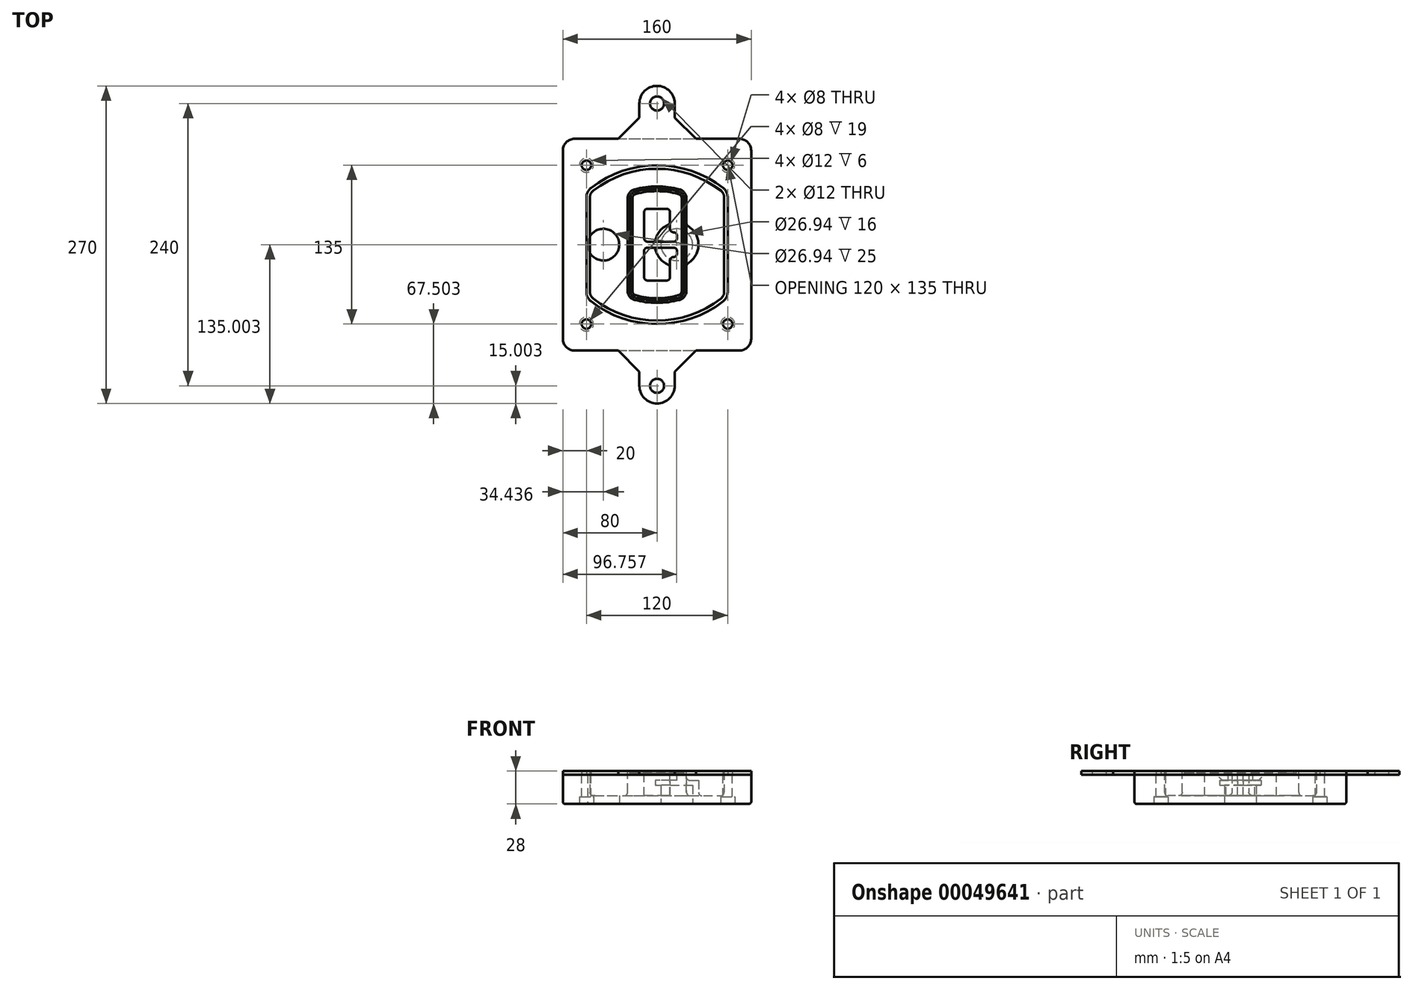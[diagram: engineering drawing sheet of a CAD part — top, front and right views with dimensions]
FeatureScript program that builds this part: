
annotation { "Feature Type Name" : "Feature", "Feature Type Description" : "" }
export const myFeature = defineFeature(function(context is Context, id is Id, definition is map)
    precondition{}
    {
        {
            var Q0;
            Q0=qCreatedBy(makeId("Top.planeOp"),FACE);
            var sketch = newSketch(context, id + "F0", { "sketchPlane" : qUnion([Q0])});
            skPoint(sketch, "E0.rect.middle", {"position": v(0, 0) * mm});
            skLineSegment(sketch, "E1.bottom", {"start": v(24.05, 28.38) * mm, "end": v(164.05, 28.38) * mm});
            skLineSegment(sketch, "E1.top", {"start": v(24.05, 208.38) * mm, "end": v(164.05, 208.38) * mm});
            skLineSegment(sketch, "E1.left", {"start": v(14.05, 38.38) * mm, "end": v(14.05, 198.38) * mm});
            skLineSegment(sketch, "E1.right", {"start": v(174.05, 38.38) * mm, "end": v(174.05, 198.38) * mm});
            skLineSegment(sketch, "E2", {"start": v(14.05, 208.38) * mm, "end": v(174.05, 28.38) * mm, "construction": true});
            skLineSegment(sketch, "E3", {"start": v(174.05, 208.38) * mm, "end": v(14.05, 28.38) * mm, "construction": true});
            skCircle(sketch, "E4", {"center": v(34.05, 185.88) * mm, "radius": 4 * mm});
            skCircle(sketch, "E5", {"center": v(154.05, 185.88) * mm, "radius": 4 * mm});
            skCircle(sketch, "E6", {"center": v(154.05, 50.88) * mm, "radius": 4 * mm});
            skCircle(sketch, "E7", {"center": v(34.05, 50.88) * mm, "radius": 4 * mm});
            skLineSegment(sketch, "E8", {"start": v(34.05, 185.88) * mm, "end": v(154.05, 185.88) * mm, "construction": true});
            skLineSegment(sketch, "E9", {"start": v(154.05, 185.88) * mm, "end": v(154.05, 50.88) * mm, "construction": true});
            skLineSegment(sketch, "E10", {"start": v(154.05, 50.88) * mm, "end": v(34.05, 50.88) * mm, "construction": true});
            skLineSegment(sketch, "E11", {"start": v(34.05, 50.88) * mm, "end": v(34.05, 185.88) * mm, "construction": true});
            skLineSegment(sketch, "E12", {"start": v(34.05, 158.68) * mm, "end": v(34.05, 78.09) * mm});
            skLineSegment(sketch, "E13", {"start": v(154.05, 158.68) * mm, "end": v(154.05, 78.09) * mm});
            skArc(sketch, "E14", {"start": v(150.2, 166.56) * mm, "mid": v(94.05, 185.88) * mm, "end": v(37.9, 166.56) * mm});
            skArc(sketch, "E15", {"start": v(37.9, 70.2) * mm, "mid": v(94.05, 50.88) * mm, "end": v(150.2, 70.2) * mm});
            skLineSegment(sketch, "E16", {"start": v(34.05, 118.38) * mm, "end": v(154.05, 118.38) * mm, "construction": true});
            skPoint(sketch, "E17.visualSharp", {"position": v(34.05, 73.38) * mm});
            skArc(sketch, "E17.filletArc", {"start": v(34.05, 78.09) * mm, "mid": v(35.06, 73.7) * mm, "end": v(37.9, 70.2) * mm});
            skPoint(sketch, "E18.visualSharp", {"position": v(34.05, 163.38) * mm});
            skArc(sketch, "E18.filletArc", {"start": v(37.9, 166.56) * mm, "mid": v(35.06, 163.06) * mm, "end": v(34.05, 158.68) * mm});
            skPoint(sketch, "E19.visualSharp", {"position": v(154.05, 163.38) * mm});
            skArc(sketch, "E19.filletArc", {"start": v(154.05, 158.68) * mm, "mid": v(153.04, 163.06) * mm, "end": v(150.2, 166.56) * mm});
            skPoint(sketch, "E20.visualSharp", {"position": v(154.05, 73.38) * mm});
            skArc(sketch, "E20.filletArc", {"start": v(150.2, 70.2) * mm, "mid": v(153.04, 73.7) * mm, "end": v(154.05, 78.09) * mm});
            skPoint(sketch, "E21.visualSharp", {"position": v(14.05, 208.38) * mm});
            skArc(sketch, "E21.filletArc", {"start": v(24.05, 208.38) * mm, "mid": v(16.98, 205.45) * mm, "end": v(14.05, 198.38) * mm});
            skPoint(sketch, "E22.visualSharp", {"position": v(174.05, 208.38) * mm});
            skArc(sketch, "E22.filletArc", {"start": v(174.05, 198.38) * mm, "mid": v(171.12, 205.45) * mm, "end": v(164.05, 208.38) * mm});
            skPoint(sketch, "E23.visualSharp", {"position": v(174.05, 28.38) * mm});
            skArc(sketch, "E23.filletArc", {"start": v(164.05, 28.38) * mm, "mid": v(171.12, 31.31) * mm, "end": v(174.05, 38.38) * mm});
            skPoint(sketch, "E24.visualSharp", {"position": v(14.05, 28.38) * mm});
            skArc(sketch, "E24.filletArc", {"start": v(14.05, 38.38) * mm, "mid": v(16.98, 31.31) * mm, "end": v(24.05, 28.38) * mm});
            skArc(sketch, "E25.0", {"start": v(151.05, 158.68) * mm, "mid": v(150.34, 161.75) * mm, "end": v(148.36, 164.2) * mm});
            skLineSegment(sketch, "E25.1", {"start": v(151.05, 158.68) * mm, "end": v(151.05, 78.09) * mm});
            skArc(sketch, "E25.2", {"start": v(148.36, 72.57) * mm, "mid": v(150.34, 75.02) * mm, "end": v(151.05, 78.09) * mm});
            skArc(sketch, "E25.3", {"start": v(39.74, 72.57) * mm, "mid": v(94.05, 53.88) * mm, "end": v(148.36, 72.57) * mm});
            skArc(sketch, "E25.4", {"start": v(37.05, 78.09) * mm, "mid": v(37.76, 75.02) * mm, "end": v(39.74, 72.57) * mm});
            skArc(sketch, "E25.5", {"start": v(148.36, 164.2) * mm, "mid": v(94.05, 182.88) * mm, "end": v(39.74, 164.2) * mm});
            skLineSegment(sketch, "E25.6", {"start": v(37.05, 158.68) * mm, "end": v(37.05, 78.09) * mm});
            skArc(sketch, "E25.7", {"start": v(39.74, 164.2) * mm, "mid": v(37.76, 161.75) * mm, "end": v(37.05, 158.68) * mm});
            skArc(sketch, "E26.0", {"start": v(35.43, 169.71) * mm, "mid": v(31.47, 164.82) * mm, "end": v(30.05, 158.68) * mm});
            skArc(sketch, "E26.1", {"start": v(152.67, 169.71) * mm, "mid": v(94.05, 189.88) * mm, "end": v(35.43, 169.71) * mm});
            skArc(sketch, "E26.2", {"start": v(158.05, 158.68) * mm, "mid": v(156.63, 164.82) * mm, "end": v(152.67, 169.71) * mm});
            skLineSegment(sketch, "E26.3", {"start": v(158.05, 158.68) * mm, "end": v(158.05, 78.09) * mm});
            skArc(sketch, "E26.4", {"start": v(152.67, 67.05) * mm, "mid": v(156.63, 71.95) * mm, "end": v(158.05, 78.09) * mm});
            skLineSegment(sketch, "E26.5", {"start": v(30.05, 158.68) * mm, "end": v(30.05, 78.09) * mm});
            skArc(sketch, "E26.6", {"start": v(35.43, 67.05) * mm, "mid": v(94.05, 46.88) * mm, "end": v(152.67, 67.05) * mm});
            skArc(sketch, "E26.7", {"start": v(30.05, 78.09) * mm, "mid": v(31.47, 71.95) * mm, "end": v(35.43, 67.05) * mm});
            skSolve(sketch);
        }
        {
            var Q0;
            Q0=makeQuery(id+"F0.imprint","IMPRINT",FACE,{"disambiguationData":[TD([[makeQuery(id+"F0.imprint","IMPRINT",EDGE,{"derivedFrom":sQuery(id+"F0.wireOp",EDGE,"E1.bottom")}),1.0]])]});
            var Q1;
            Q1=makeQuery(id+"F0.imprint","IMPRINT",FACE,{"disambiguationData":[TD([[makeQuery(id+"F0.imprint","IMPRINT",EDGE,{"derivedFrom":sQuery(id+"F0.wireOp",EDGE,"E12")}),1.0]])]});
            var Q2;
            Q2=makeQuery(id+"F0.imprint","IMPRINT",FACE,{"disambiguationData":[TD([[makeQuery(id+"F0.imprint","IMPRINT",EDGE,{"derivedFrom":sQuery(id+"F0.wireOp",EDGE,"E25.0")}),1.0]])]});
            var Q3;
            Q3=makeQuery(id+"F0.imprint","IMPRINT",FACE,{"disambiguationData":[TD([[makeQuery(id+"F0.imprint","IMPRINT",EDGE,{"derivedFrom":sQuery(id+"F0.wireOp",EDGE,"E12")}),-1.0]])]});
            extrude(context, id + "F1", {"entities" : qUnion([Q0, Q1, Q2, Q3]), "oppositeDirection" : true, "depth" : 25 * mm});
        }
        {
            var Q0;
            Q0=makeQuery(id+"F0.imprint","IMPRINT",FACE,{"disambiguationData":[TD([[makeQuery(id+"F0.imprint","IMPRINT",EDGE,{"derivedFrom":sQuery(id+"F0.wireOp",EDGE,"E12")}),1.0]])]});
            extrude(context, id + "F2", {"entities" : qUnion([Q0]), "operationType" : NewBodyOperationType.ADD, "depth" : 3 * mm});
        }
        {
            var Q0;
            Q0=makeQuery(id+"F0.imprint","IMPRINT",FACE,{"disambiguationData":[TD([[makeQuery(id+"F0.imprint","IMPRINT",EDGE,{"derivedFrom":sQuery(id+"F0.wireOp",EDGE,"E25.0")}),1.0]])]});
            extrude(context, id + "F3", {"entities" : qUnion([Q0]), "operationType" : NewBodyOperationType.REMOVE, "oppositeDirection" : true, "depth" : 18 * mm});
        }
        {
            var Q0;
            Q0=makeQuery(id+"F2.opExtrude","CAP_FACE",FACE,{"disambiguationData":[OSD([sQuery(id+"F0.wireOp",EDGE,"E12"),sQuery(id+"F0.wireOp",EDGE,"E13"),sQuery(id+"F0.wireOp",EDGE,"E14"),sQuery(id+"F0.wireOp",EDGE,"E15"),sQuery(id+"F0.wireOp",EDGE,"E17.filletArc"),sQuery(id+"F0.wireOp",EDGE,"E18.filletArc"),sQuery(id+"F0.wireOp",EDGE,"E19.filletArc"),sQuery(id+"F0.wireOp",EDGE,"E20.filletArc"),sQuery(id+"F0.wireOp",EDGE,"E25.0"),sQuery(id+"F0.wireOp",EDGE,"E25.1"),sQuery(id+"F0.wireOp",EDGE,"E25.2"),sQuery(id+"F0.wireOp",EDGE,"E25.3"),sQuery(id+"F0.wireOp",EDGE,"E25.4"),sQuery(id+"F0.wireOp",EDGE,"E25.5"),sQuery(id+"F0.wireOp",EDGE,"E25.6"),sQuery(id+"F0.wireOp",EDGE,"E25.7")])],"isStart":false});
            var sketch = newSketch(context, id + "F4", { "sketchPlane" : qUnion([Q0])});
            skArc(sketch, "E27.0", {"start": v(74.97, 71.41) * mm, "mid": v(94.05, 68.88) * mm, "end": v(113.13, 71.41) * mm});
            skArc(sketch, "E28.0", {"start": v(113.13, 165.35) * mm, "mid": v(94.05, 167.88) * mm, "end": v(74.97, 165.35) * mm});
            skLineSegment(sketch, "E29", {"start": v(69.05, 157.63) * mm, "end": v(69.05, 79.14) * mm});
            skLineSegment(sketch, "E30", {"start": v(119.05, 157.63) * mm, "end": v(119.05, 79.14) * mm});
            skLineSegment(sketch, "E31", {"start": v(69.05, 163.48) * mm, "end": v(119.05, 163.48) * mm, "construction": true});
            skLineSegment(sketch, "E32", {"start": v(69.05, 73.28) * mm, "end": v(119.05, 73.28) * mm, "construction": true});
            skPoint(sketch, "E33.visualSharp", {"position": v(69.05, 163.48) * mm});
            skArc(sketch, "E33.filletArc", {"start": v(74.97, 165.35) * mm, "mid": v(70.7, 162.5) * mm, "end": v(69.05, 157.63) * mm});
            skPoint(sketch, "E34.visualSharp", {"position": v(119.05, 163.48) * mm});
            skArc(sketch, "E34.filletArc", {"start": v(119.05, 157.63) * mm, "mid": v(117.4, 162.5) * mm, "end": v(113.13, 165.35) * mm});
            skPoint(sketch, "E35.visualSharp", {"position": v(119.05, 73.28) * mm});
            skArc(sketch, "E35.filletArc", {"start": v(113.13, 71.41) * mm, "mid": v(117.4, 74.27) * mm, "end": v(119.05, 79.14) * mm});
            skPoint(sketch, "E36.visualSharp", {"position": v(69.05, 73.28) * mm});
            skArc(sketch, "E36.filletArc", {"start": v(69.05, 79.14) * mm, "mid": v(70.7, 74.27) * mm, "end": v(74.97, 71.41) * mm});
            skArc(sketch, "E37.0", {"start": v(148.36, 164.2) * mm, "mid": v(94.05, 182.88) * mm, "end": v(39.74, 164.2) * mm});
            skArc(sketch, "E37.1", {"start": v(39.74, 164.2) * mm, "mid": v(37.76, 161.75) * mm, "end": v(37.05, 158.68) * mm});
            skLineSegment(sketch, "E37.2", {"start": v(37.05, 158.68) * mm, "end": v(37.05, 78.09) * mm});
            skArc(sketch, "E37.3", {"start": v(37.05, 78.09) * mm, "mid": v(37.76, 75.02) * mm, "end": v(39.74, 72.57) * mm});
            skArc(sketch, "E37.4", {"start": v(39.74, 72.57) * mm, "mid": v(94.05, 53.88) * mm, "end": v(148.36, 72.57) * mm});
            skArc(sketch, "E37.5", {"start": v(148.36, 72.57) * mm, "mid": v(150.34, 75.02) * mm, "end": v(151.05, 78.09) * mm});
            skLineSegment(sketch, "E37.6", {"start": v(151.05, 158.68) * mm, "end": v(151.05, 78.09) * mm});
            skArc(sketch, "E37.7", {"start": v(151.05, 158.68) * mm, "mid": v(150.34, 161.75) * mm, "end": v(148.36, 164.2) * mm});
            skLineSegment(sketch, "E38.0", {"start": v(117.05, 157.63) * mm, "end": v(117.05, 79.14) * mm});
            skArc(sketch, "E38.1", {"start": v(112.61, 73.34) * mm, "mid": v(115.81, 75.49) * mm, "end": v(117.05, 79.14) * mm});
            skArc(sketch, "E38.2", {"start": v(75.49, 73.34) * mm, "mid": v(94.05, 70.88) * mm, "end": v(112.61, 73.34) * mm});
            skArc(sketch, "E38.3", {"start": v(71.05, 79.14) * mm, "mid": v(72.29, 75.49) * mm, "end": v(75.49, 73.34) * mm});
            skLineSegment(sketch, "E38.4", {"start": v(71.05, 157.63) * mm, "end": v(71.05, 79.14) * mm});
            skArc(sketch, "E38.5", {"start": v(117.05, 157.63) * mm, "mid": v(115.81, 161.28) * mm, "end": v(112.61, 163.42) * mm});
            skArc(sketch, "E38.6", {"start": v(75.49, 163.42) * mm, "mid": v(72.29, 161.28) * mm, "end": v(71.05, 157.63) * mm});
            skArc(sketch, "E38.7", {"start": v(112.61, 163.42) * mm, "mid": v(94.05, 165.88) * mm, "end": v(75.49, 163.42) * mm});
            skArc(sketch, "E39.0", {"start": v(115.05, 157.63) * mm, "mid": v(114.23, 160.06) * mm, "end": v(112.1, 161.5) * mm});
            skLineSegment(sketch, "E39.1", {"start": v(115.05, 157.63) * mm, "end": v(115.05, 79.14) * mm});
            skArc(sketch, "E39.2", {"start": v(112.1, 75.27) * mm, "mid": v(114.23, 76.7) * mm, "end": v(115.05, 79.14) * mm});
            skArc(sketch, "E39.3", {"start": v(76, 75.27) * mm, "mid": v(94.05, 72.88) * mm, "end": v(112.1, 75.27) * mm});
            skArc(sketch, "E39.4", {"start": v(73.05, 79.14) * mm, "mid": v(73.87, 76.7) * mm, "end": v(76, 75.27) * mm});
            skArc(sketch, "E39.5", {"start": v(112.1, 161.5) * mm, "mid": v(94.05, 163.88) * mm, "end": v(76, 161.5) * mm});
            skLineSegment(sketch, "E39.6", {"start": v(73.05, 157.63) * mm, "end": v(73.05, 79.14) * mm});
            skArc(sketch, "E39.7", {"start": v(76, 161.5) * mm, "mid": v(73.87, 160.06) * mm, "end": v(73.05, 157.63) * mm});
            skLineSegment(sketch, "E40", {"start": v(69.05, 118.38) * mm, "end": v(119.05, 118.38) * mm, "construction": true});
            skLineSegment(sketch, "E41", {"start": v(83.05, 123.88) * mm, "end": v(83.05, 145.88) * mm});
            skLineSegment(sketch, "E42", {"start": v(86.05, 148.88) * mm, "end": v(102.05, 148.88) * mm});
            skLineSegment(sketch, "E43", {"start": v(105.05, 145.88) * mm, "end": v(105.05, 131.88) * mm});
            skLineSegment(sketch, "E44", {"start": v(108.05, 128.88) * mm, "end": v(108.05, 128.88) * mm});
            skLineSegment(sketch, "E45", {"start": v(111.05, 125.88) * mm, "end": v(111.05, 123.88) * mm});
            skLineSegment(sketch, "E46", {"start": v(108.05, 120.88) * mm, "end": v(86.05, 120.88) * mm});
            skPoint(sketch, "E47.visualSharp", {"position": v(83.05, 148.88) * mm});
            skArc(sketch, "E47.filletArc", {"start": v(86.05, 148.88) * mm, "mid": v(83.93, 148) * mm, "end": v(83.05, 145.88) * mm});
            skPoint(sketch, "E48.visualSharp", {"position": v(105.05, 148.88) * mm});
            skArc(sketch, "E48.filletArc", {"start": v(105.05, 145.88) * mm, "mid": v(104.17, 148) * mm, "end": v(102.05, 148.88) * mm});
            skPoint(sketch, "E49.visualSharp", {"position": v(105.05, 128.88) * mm});
            skArc(sketch, "E49.filletArc", {"start": v(105.05, 131.88) * mm, "mid": v(105.93, 129.76) * mm, "end": v(108.05, 128.88) * mm});
            skPoint(sketch, "E50.visualSharp", {"position": v(111.05, 128.88) * mm});
            skArc(sketch, "E50.filletArc", {"start": v(111.05, 125.88) * mm, "mid": v(110.17, 128) * mm, "end": v(108.05, 128.88) * mm});
            skPoint(sketch, "E51.visualSharp", {"position": v(111.05, 120.88) * mm});
            skArc(sketch, "E51.filletArc", {"start": v(108.05, 120.88) * mm, "mid": v(110.17, 121.76) * mm, "end": v(111.05, 123.88) * mm});
            skPoint(sketch, "E52.visualSharp", {"position": v(83.05, 120.88) * mm});
            skArc(sketch, "E52.filletArc", {"start": v(83.05, 123.88) * mm, "mid": v(83.93, 121.76) * mm, "end": v(86.05, 120.88) * mm});
            skLineSegment(sketch, "E53.0.MirrorCS", {"start": v(108.05, 115.88) * mm, "end": v(86.05, 115.88) * mm});
            skArc(sketch, "E54.0.MirrorCS", {"start": v(83.05, 112.88) * mm, "mid": v(83.93, 115) * mm, "end": v(86.05, 115.88) * mm});
            skLineSegment(sketch, "E55.0.MirrorCS", {"start": v(83.05, 112.88) * mm, "end": v(83.05, 90.88) * mm});
            skArc(sketch, "E56.0.MirrorCS", {"start": v(86.05, 87.88) * mm, "mid": v(83.93, 88.76) * mm, "end": v(83.05, 90.88) * mm});
            skLineSegment(sketch, "E57.0.MirrorCS", {"start": v(86.05, 87.88) * mm, "end": v(102.05, 87.88) * mm});
            skArc(sketch, "E58.0.MirrorCS", {"start": v(105.05, 90.88) * mm, "mid": v(104.17, 88.76) * mm, "end": v(102.05, 87.88) * mm});
            skLineSegment(sketch, "E59.0.MirrorCS", {"start": v(105.05, 90.88) * mm, "end": v(105.05, 104.88) * mm});
            skArc(sketch, "E60.0.MirrorCS", {"start": v(105.05, 104.88) * mm, "mid": v(105.93, 107) * mm, "end": v(108.05, 107.88) * mm});
            skArc(sketch, "E61.0.MirrorCS", {"start": v(111.05, 110.88) * mm, "mid": v(110.17, 108.76) * mm, "end": v(108.05, 107.88) * mm});
            skLineSegment(sketch, "E62.0.MirrorCS", {"start": v(111.05, 110.88) * mm, "end": v(111.05, 112.88) * mm});
            skArc(sketch, "E63.0.MirrorCS", {"start": v(108.05, 115.88) * mm, "mid": v(110.17, 115) * mm, "end": v(111.05, 112.88) * mm});
            skSolve(sketch);
        }
        {
            var Q0;
            Q0=makeQuery(id+"F4.imprint","IMPRINT",FACE,{"disambiguationData":[TD([[makeQuery(id+"F4.imprint","IMPRINT",EDGE,{"derivedFrom":sQuery(id+"F4.wireOp",EDGE,"E27.0")}),1.0]])]});
            var Q1;
            Q1=makeQuery(id+"F4.imprint","IMPRINT",FACE,{"disambiguationData":[TD([[makeQuery(id+"F4.imprint","IMPRINT",EDGE,{"derivedFrom":sQuery(id+"F4.wireOp",EDGE,"E38.0")}),-1.0]])]});
            var Q2;
            Q2=makeQuery(id+"F4.imprint","IMPRINT",FACE,{"disambiguationData":[TD([[makeQuery(id+"F4.imprint","IMPRINT",EDGE,{"derivedFrom":sQuery(id+"F4.wireOp",EDGE,"E39.0")}),1.0]])]});
            extrude(context, id + "F5", {"entities" : qUnion([Q0, Q1, Q2]), "operationType" : NewBodyOperationType.ADD, "endBound" : BoundingType.UP_TO_NEXT, "oppositeDirection" : true, "depth" : 25 * mm});
        }
        {
            var Q0;
            Q0=makeQuery(id+"F4.imprint","IMPRINT",FACE,{"disambiguationData":[TD([[makeQuery(id+"F4.imprint","IMPRINT",EDGE,{"derivedFrom":sQuery(id+"F4.wireOp",EDGE,"E38.0")}),-1.0]])]});
            extrude(context, id + "F6", {"entities" : qUnion([Q0]), "operationType" : NewBodyOperationType.REMOVE, "oppositeDirection" : true, "depth" : 2 * mm});
        }
        {
            var Q0;
            Q0=makeQuery(id+"F1.opExtrude","CAP_FACE",FACE,{"disambiguationData":[OSD([sQuery(id+"F0.wireOp",EDGE,"E1.bottom"),sQuery(id+"F0.wireOp",EDGE,"E1.top"),sQuery(id+"F0.wireOp",EDGE,"E1.left"),sQuery(id+"F0.wireOp",EDGE,"E1.right"),sQuery(id+"F0.wireOp",EDGE,"E4"),sQuery(id+"F0.wireOp",EDGE,"E5"),sQuery(id+"F0.wireOp",EDGE,"E6"),sQuery(id+"F0.wireOp",EDGE,"E7"),sQuery(id+"F0.wireOp",EDGE,"E21.filletArc"),sQuery(id+"F0.wireOp",EDGE,"E22.filletArc"),sQuery(id+"F0.wireOp",EDGE,"E23.filletArc"),sQuery(id+"F0.wireOp",EDGE,"E24.filletArc")])],"isStart":false});
            var sketch = newSketch(context, id + "F7", { "sketchPlane" : qUnion([Q0])});
            skCircle(sketch, "E64", {"center": v(110.8, -118.38) * mm, "radius": 13.47 * mm});
            skCircle(sketch, "E65", {"center": v(48.49, -118.38) * mm, "radius": 13.47 * mm});
            skLineSegment(sketch, "E66", {"start": v(174.05, -118.38) * mm, "end": v(14.05, -118.38) * mm});
            skCircle(sketch, "E67", {"center": v(110.8, -118.38) * mm, "radius": 18.47 * mm});
            skCircle(sketch, "E68", {"center": v(154.05, -185.88) * mm, "radius": 6 * mm});
            skCircle(sketch, "E69", {"center": v(34.05, -185.88) * mm, "radius": 6 * mm});
            skCircle(sketch, "E70", {"center": v(34.05, -50.88) * mm, "radius": 6 * mm});
            skCircle(sketch, "E71", {"center": v(154.05, -50.88) * mm, "radius": 6 * mm});
            skSolve(sketch);
        }
        {
            var Q0;
            {var subQ1=sQuery(id+"F7.wireOp",EDGE,"E66");var subQ4=sQuery(id+"F7.wireOp",EDGE,"E64");var subQ6=makeQuery(id+"F7.imprint","INTERSECT",VERTEX,{"disambiguationData":[OD(0.0)],"derivedFrom":[subQ4,subQ1]});Q0=makeQuery(id+"F7.imprint","IMPRINT",FACE,{"disambiguationData":[TD([[makeQuery(id+"F7.imprint","IMPRINT",EDGE,{"disambiguationData":[TD([[subQ6,-1.0]])],"derivedFrom":subQ4}),-1.0]])]});}
            var Q1;
            {var subQ0=sQuery(id+"F7.wireOp",EDGE,"E66");var subQ1=sQuery(id+"F7.wireOp",EDGE,"E64");var subQ3=makeQuery(id+"F7.imprint","INTERSECT",VERTEX,{"disambiguationData":[OD(0.0)],"derivedFrom":[subQ1,subQ0]});Q1=makeQuery(id+"F7.imprint","IMPRINT",FACE,{"disambiguationData":[TD([[makeQuery(id+"F7.imprint","IMPRINT",EDGE,{"disambiguationData":[TD([[subQ3,-1.0]])],"derivedFrom":subQ1}),1.0]])]});}
            var Q2;
            {var subQ0=sQuery(id+"F7.wireOp",EDGE,"E66");var subQ1=sQuery(id+"F7.wireOp",EDGE,"E64");var subQ3=makeQuery(id+"F7.imprint","INTERSECT",VERTEX,{"disambiguationData":[OD(0.0)],"derivedFrom":[subQ1,subQ0]});Q2=makeQuery(id+"F7.imprint","IMPRINT",FACE,{"disambiguationData":[TD([[makeQuery(id+"F7.imprint","IMPRINT",EDGE,{"disambiguationData":[TD([[subQ3,1.0]])],"derivedFrom":subQ1}),1.0]])]});}
            var Q3;
            {var subQ1=sQuery(id+"F7.wireOp",EDGE,"E66");var subQ4=sQuery(id+"F7.wireOp",EDGE,"E64");var subQ6=makeQuery(id+"F7.imprint","INTERSECT",VERTEX,{"disambiguationData":[OD(0.0)],"derivedFrom":[subQ4,subQ1]});Q3=makeQuery(id+"F7.imprint","IMPRINT",FACE,{"disambiguationData":[TD([[makeQuery(id+"F7.imprint","IMPRINT",EDGE,{"disambiguationData":[TD([[subQ6,1.0]])],"derivedFrom":subQ4}),-1.0]])]});}
            extrude(context, id + "F8", {"entities" : qUnion([Q0, Q1, Q2, Q3]), "operationType" : NewBodyOperationType.ADD, "oppositeDirection" : true, "depth" : 20 * mm});
        }
        {
            var Q0;
            {var subQ0=sQuery(id+"F7.wireOp",EDGE,"E66");var subQ1=sQuery(id+"F7.wireOp",EDGE,"E64");var subQ3=makeQuery(id+"F7.imprint","INTERSECT",VERTEX,{"disambiguationData":[OD(0.0)],"derivedFrom":[subQ1,subQ0]});Q0=makeQuery(id+"F7.imprint","IMPRINT",FACE,{"disambiguationData":[TD([[makeQuery(id+"F7.imprint","IMPRINT",EDGE,{"disambiguationData":[TD([[subQ3,-1.0]])],"derivedFrom":subQ1}),1.0]])]});}
            var Q1;
            {var subQ0=sQuery(id+"F7.wireOp",EDGE,"E66");var subQ1=sQuery(id+"F7.wireOp",EDGE,"E64");var subQ3=makeQuery(id+"F7.imprint","INTERSECT",VERTEX,{"disambiguationData":[OD(0.0)],"derivedFrom":[subQ1,subQ0]});Q1=makeQuery(id+"F7.imprint","IMPRINT",FACE,{"disambiguationData":[TD([[makeQuery(id+"F7.imprint","IMPRINT",EDGE,{"disambiguationData":[TD([[subQ3,1.0]])],"derivedFrom":subQ1}),1.0]])]});}
            extrude(context, id + "F9", {"entities" : qUnion([Q0, Q1]), "operationType" : NewBodyOperationType.REMOVE, "oppositeDirection" : true, "depth" : 16 * mm});
        }
        {
            var Q0;
            {var subQ0=sQuery(id+"F7.wireOp",EDGE,"E66");var subQ1=sQuery(id+"F7.wireOp",EDGE,"E65");var subQ3=makeQuery(id+"F7.imprint","INTERSECT",VERTEX,{"disambiguationData":[OD(0.0)],"derivedFrom":[subQ1,subQ0]});Q0=makeQuery(id+"F7.imprint","IMPRINT",FACE,{"disambiguationData":[TD([[makeQuery(id+"F7.imprint","IMPRINT",EDGE,{"disambiguationData":[TD([[subQ3,-1.0]])],"derivedFrom":subQ1}),1.0]])]});}
            var Q1;
            {var subQ0=sQuery(id+"F7.wireOp",EDGE,"E66");var subQ1=sQuery(id+"F7.wireOp",EDGE,"E65");var subQ3=makeQuery(id+"F7.imprint","INTERSECT",VERTEX,{"disambiguationData":[OD(0.0)],"derivedFrom":[subQ1,subQ0]});Q1=makeQuery(id+"F7.imprint","IMPRINT",FACE,{"disambiguationData":[TD([[makeQuery(id+"F7.imprint","IMPRINT",EDGE,{"disambiguationData":[TD([[subQ3,1.0]])],"derivedFrom":subQ1}),1.0]])]});}
            extrude(context, id + "F10", {"entities" : qUnion([Q0, Q1]), "operationType" : NewBodyOperationType.REMOVE, "oppositeDirection" : true, "depth" : 25 * mm});
        }
        {
            var Q0;
            Q0=makeQuery(id+"F7.imprint","IMPRINT",FACE,{"disambiguationData":[TD([[makeQuery(id+"F7.imprint","IMPRINT",EDGE,{"derivedFrom":sQuery(id+"F7.wireOp",EDGE,"E68")}),1.0]])]});
            var Q1;
            Q1=makeQuery(id+"F7.imprint","IMPRINT",FACE,{"disambiguationData":[TD([[makeQuery(id+"F7.imprint","IMPRINT",EDGE,{"derivedFrom":makeQuery(id+"F1.opExtrude","CAP_EDGE",EDGE,{"disambiguationData":[OSD([sQuery(id+"F0.wireOp",EDGE,"E5")])],"isStart":false})}),-1.0]])]});
            var Q2;
            Q2=makeQuery(id+"F7.imprint","IMPRINT",FACE,{"disambiguationData":[TD([[makeQuery(id+"F7.imprint","IMPRINT",EDGE,{"derivedFrom":sQuery(id+"F7.wireOp",EDGE,"E69")}),1.0]])]});
            var Q3;
            Q3=makeQuery(id+"F7.imprint","IMPRINT",FACE,{"disambiguationData":[TD([[makeQuery(id+"F7.imprint","IMPRINT",EDGE,{"derivedFrom":makeQuery(id+"F1.opExtrude","CAP_EDGE",EDGE,{"disambiguationData":[OSD([sQuery(id+"F0.wireOp",EDGE,"E4")])],"isStart":false})}),-1.0]])]});
            var Q4;
            Q4=makeQuery(id+"F7.imprint","IMPRINT",FACE,{"disambiguationData":[TD([[makeQuery(id+"F7.imprint","IMPRINT",EDGE,{"derivedFrom":sQuery(id+"F7.wireOp",EDGE,"E70")}),1.0]])]});
            var Q5;
            Q5=makeQuery(id+"F7.imprint","IMPRINT",FACE,{"disambiguationData":[TD([[makeQuery(id+"F7.imprint","IMPRINT",EDGE,{"derivedFrom":makeQuery(id+"F1.opExtrude","CAP_EDGE",EDGE,{"disambiguationData":[OSD([sQuery(id+"F0.wireOp",EDGE,"E7")])],"isStart":false})}),-1.0]])]});
            var Q6;
            Q6=makeQuery(id+"F7.imprint","IMPRINT",FACE,{"disambiguationData":[TD([[makeQuery(id+"F7.imprint","IMPRINT",EDGE,{"derivedFrom":sQuery(id+"F7.wireOp",EDGE,"E71")}),1.0]])]});
            var Q7;
            Q7=makeQuery(id+"F7.imprint","IMPRINT",FACE,{"disambiguationData":[TD([[makeQuery(id+"F7.imprint","IMPRINT",EDGE,{"derivedFrom":makeQuery(id+"F1.opExtrude","CAP_EDGE",EDGE,{"disambiguationData":[OSD([sQuery(id+"F0.wireOp",EDGE,"E6")])],"isStart":false})}),-1.0]])]});
            extrude(context, id + "F11", {"entities" : qUnion([Q0, Q1, Q2, Q3, Q4, Q5, Q6, Q7]), "operationType" : NewBodyOperationType.REMOVE, "oppositeDirection" : true, "depth" : 6 * mm});
        }
        {
            var Q0;
            Q0=makeQuery(id+"F9.boolean.opBoolean","COPY",FACE,{"derivedFrom":makeQuery(id+"F9.opExtrude","CAP_FACE",FACE,{"disambiguationData":[OSD([sQuery(id+"F7.wireOp",EDGE,"E64")])],"isStart":false})});
            var sketch = newSketch(context, id + "F12", { "sketchPlane" : qUnion([Q0])});
            skArc(sketch, "E72.0", {"start": v(105.05, -100.83) * mm, "mid": v(96.62, -106.56) * mm, "end": v(92.5, -115.88) * mm});
            skArc(sketch, "E72.1", {"start": v(92.5, -120.88) * mm, "mid": v(96.62, -130.2) * mm, "end": v(105.05, -135.93) * mm});
            skLineSegment(sketch, "E73", {"start": v(92.5, -120.88) * mm, "end": v(108.05, -120.88) * mm});
            skLineSegment(sketch, "E74.0", {"start": v(108.05, -115.88) * mm, "end": v(92.5, -115.88) * mm});
            skArc(sketch, "E74.1", {"start": v(108.05, -115.88) * mm, "mid": v(110.17, -115) * mm, "end": v(111.05, -112.88) * mm});
            skLineSegment(sketch, "E74.2", {"start": v(111.05, -110.88) * mm, "end": v(111.05, -112.88) * mm});
            skArc(sketch, "E74.3", {"start": v(111.05, -110.88) * mm, "mid": v(110.17, -108.76) * mm, "end": v(108.05, -107.88) * mm});
            skArc(sketch, "E74.4", {"start": v(105.05, -104.88) * mm, "mid": v(105.93, -107) * mm, "end": v(108.05, -107.88) * mm});
            skLineSegment(sketch, "E74.5", {"start": v(105.05, -100.83) * mm, "end": v(105.05, -104.88) * mm});
            skLineSegment(sketch, "E74.7", {"start": v(108.05, -120.88) * mm, "end": v(92.5, -120.88) * mm});
            skArc(sketch, "E74.8", {"start": v(108.05, -120.88) * mm, "mid": v(110.17, -121.76) * mm, "end": v(111.05, -123.88) * mm});
            skLineSegment(sketch, "E74.9", {"start": v(111.05, -125.88) * mm, "end": v(111.05, -123.88) * mm});
            skArc(sketch, "E74.10", {"start": v(111.05, -125.88) * mm, "mid": v(110.17, -128) * mm, "end": v(108.05, -128.88) * mm});
            skArc(sketch, "E74.11", {"start": v(105.05, -131.88) * mm, "mid": v(105.93, -129.76) * mm, "end": v(108.05, -128.88) * mm});
            skLineSegment(sketch, "E74.12", {"start": v(105.05, -135.93) * mm, "end": v(105.05, -131.88) * mm});
            skPoint(sketch, "E75.orphan", {"position": v(105.05, -145.88) * mm});
            skPoint(sketch, "E76.orphan", {"position": v(86.05, -120.88) * mm});
            skPoint(sketch, "E77.orphan", {"position": v(86.05, -115.88) * mm});
            skPoint(sketch, "E78.orphan", {"position": v(105.05, -90.88) * mm});
            skSolve(sketch);
        }
        {
            var Q0;
            {var subQ7=sQuery(id+"F12.wireOp",EDGE,"E72.0");var subQ14=sQuery(id+"F12.wireOp",EDGE,"E72.1");var subQ16=sQuery(id+"F12.wireOp",EDGE,"E74.1");var subQ18=sQuery(id+"F12.wireOp",EDGE,"E74.8");Q0=qUnion([makeQuery(id+"F12.imprint","IMPRINT",FACE,{"disambiguationData":[TD([[makeQuery(id+"F12.imprint","IMPRINT",EDGE,{"derivedFrom":subQ7}),1.0]])]}),makeQuery(id+"F12.imprint","IMPRINT",FACE,{"disambiguationData":[TD([[makeQuery(id+"F12.imprint","IMPRINT",EDGE,{"derivedFrom":subQ14}),1.0]])]}),makeQuery(id+"F12.imprint","IMPRINT",FACE,{"disambiguationData":[TD([[makeQuery(id+"F12.imprint","IMPRINT",EDGE,{"derivedFrom":subQ16}),1.0]])]}),makeQuery(id+"F12.imprint","IMPRINT",FACE,{"disambiguationData":[TD([[makeQuery(id+"F12.imprint","IMPRINT",EDGE,{"derivedFrom":subQ18}),-1.0]])]})]);}
            var Q1;
            Q1=makeQuery(id+"F5.boolean.opBoolean","SPLIT",FACE,{"disambiguationData":[TD([makeQuery(id+"F5.opExtrude","SWEPT_FACE",FACE,{"disambiguationData":[OSD([sQuery(id+"F4.wireOp",EDGE,"E41")])]})])],"derivedFrom":makeQuery(id+"F3.boolean.opBoolean","COPY",FACE,{"derivedFrom":makeQuery(id+"F3.opExtrude","CAP_FACE",FACE,{"disambiguationData":[OSD([sQuery(id+"F0.wireOp",EDGE,"E25.0"),sQuery(id+"F0.wireOp",EDGE,"E25.1"),sQuery(id+"F0.wireOp",EDGE,"E25.2"),sQuery(id+"F0.wireOp",EDGE,"E25.3"),sQuery(id+"F0.wireOp",EDGE,"E25.4"),sQuery(id+"F0.wireOp",EDGE,"E25.5"),sQuery(id+"F0.wireOp",EDGE,"E25.6"),sQuery(id+"F0.wireOp",EDGE,"E25.7")])],"isStart":false})})});
            extrude(context, id + "F13", {"entities" : qUnion([Q0]), "operationType" : NewBodyOperationType.REMOVE, "endBound" : BoundingType.UP_TO_SURFACE, "endBoundEntityFace" : qUnion([Q1]), "depth" : 25 * mm});
        }
        {
            var Q0;
            Q0=makeQuery(id+"F3.boolean.opBoolean","COPY",EDGE,{"derivedFrom":makeQuery(id+"F3.opExtrude","CAP_EDGE",EDGE,{"disambiguationData":[OSD([sQuery(id+"F0.wireOp",EDGE,"E25.6")])],"isStart":false})});
            var Q1;
            Q1=makeQuery(id+"F8.boolean.opBoolean","INTERSECT",EDGE,{"derivedFrom":[makeQuery(id+"F5.opExtrude","SWEPT_FACE",FACE,{"disambiguationData":[OSD([sQuery(id+"F4.wireOp",EDGE,"E30")])]}),makeQuery(id+"F8.opExtrude","CAP_FACE",FACE,{"disambiguationData":[OSD([sQuery(id+"F7.wireOp",EDGE,"E67")])],"isStart":false})]});
            var Q2;
            Q2=makeQuery(id+"F8.boolean.opBoolean","INTERSECT",EDGE,{"disambiguationData":[OD(1.0)],"derivedFrom":[makeQuery(id+"F5.opExtrude","SWEPT_FACE",FACE,{"disambiguationData":[OSD([sQuery(id+"F4.wireOp",EDGE,"E30")])]}),makeQuery(id+"F8.opExtrude","SWEPT_FACE",FACE,{"disambiguationData":[OSD([sQuery(id+"F7.wireOp",EDGE,"E67")])]})]});
            var Q3;
            {var subQ0=sQuery(id+"F4.wireOp",EDGE,"E30");Q3=makeQuery(id+"F8.boolean.opBoolean","SPLIT",EDGE,{"disambiguationData":[TD([makeQuery(id+"F5.opExtrude","SWEPT_FACE",FACE,{"disambiguationData":[OSD([sQuery(id+"F4.wireOp",EDGE,"E35.filletArc")])]})])],"derivedFrom":makeQuery(id+"F5.opExtrude","CAP_EDGE",EDGE,{"disambiguationData":[OSD([subQ0])],"isStart":false})});}
            var Q4;
            {var subQ0=sQuery(id+"F0.wireOp",EDGE,"E25.7");var subQ1=sQuery(id+"F0.wireOp",EDGE,"E25.1");var subQ2=sQuery(id+"F0.wireOp",EDGE,"E25.6");var subQ3=sQuery(id+"F0.wireOp",EDGE,"E25.5");var subQ4=sQuery(id+"F0.wireOp",EDGE,"E25.4");var subQ5=sQuery(id+"F0.wireOp",EDGE,"E25.0");var subQ6=sQuery(id+"F0.wireOp",EDGE,"E25.2");var subQ7=sQuery(id+"F0.wireOp",EDGE,"E25.3");Q4=makeQuery(id+"F8.boolean.opBoolean","INTERSECT",EDGE,{"derivedFrom":[makeQuery(id+"F5.boolean.opBoolean","SPLIT",FACE,{"disambiguationData":[TD([makeQuery(id+"F2.opExtrude","SWEPT_FACE",FACE,{"disambiguationData":[OSD([subQ5])]})])],"derivedFrom":makeQuery(id+"F3.boolean.opBoolean","COPY",FACE,{"derivedFrom":makeQuery(id+"F3.opExtrude","CAP_FACE",FACE,{"disambiguationData":[OSD([subQ5,subQ1,subQ6,subQ7,subQ4,subQ3,subQ2,subQ0])],"isStart":false})})}),makeQuery(id+"F8.opExtrude","SWEPT_FACE",FACE,{"disambiguationData":[OSD([sQuery(id+"F7.wireOp",EDGE,"E67")])]})]});}
            var Q5;
            Q5=makeQuery(id+"F8.boolean.opBoolean","INTERSECT",EDGE,{"disambiguationData":[OD(0.0)],"derivedFrom":[makeQuery(id+"F5.opExtrude","SWEPT_FACE",FACE,{"disambiguationData":[OSD([sQuery(id+"F4.wireOp",EDGE,"E30")])]}),makeQuery(id+"F8.opExtrude","SWEPT_FACE",FACE,{"disambiguationData":[OSD([sQuery(id+"F7.wireOp",EDGE,"E67")])]})]});
            fillet(context, id + "F14", {"entities" : qUnion([Q0, Q1, Q2, Q3, Q4, Q5]), "radius" : 3 * mm, "tangentPropagation" : true, "allowEdgeOverflow" : false});
        }
        {
            var Q0;
            Q0=makeQuery(id+"F1.opExtrude","CAP_EDGE",EDGE,{"disambiguationData":[OSD([sQuery(id+"F0.wireOp",EDGE,"E1.bottom")])],"isStart":false});
            fillet(context, id + "F15", {"entities" : qUnion([Q0]), "radius" : 2 * mm, "tangentPropagation" : true, "allowEdgeOverflow" : false});
        }
        {
            var Q0;
            {var subQ0=sQuery(id+"F0.wireOp",EDGE,"E1.bottom");var subQ1=sQuery(id+"F0.wireOp",EDGE,"E1.top");var subQ2=sQuery(id+"F0.wireOp",EDGE,"E1.left");var subQ3=sQuery(id+"F0.wireOp",EDGE,"E1.right");var subQ4=sQuery(id+"F0.wireOp",EDGE,"E4");var subQ5=sQuery(id+"F0.wireOp",EDGE,"E5");var subQ6=sQuery(id+"F0.wireOp",EDGE,"E6");var subQ7=sQuery(id+"F0.wireOp",EDGE,"E7");var subQ8=sQuery(id+"F0.wireOp",EDGE,"E21.filletArc");var subQ9=sQuery(id+"F0.wireOp",EDGE,"E22.filletArc");var subQ10=sQuery(id+"F0.wireOp",EDGE,"E23.filletArc");var subQ11=sQuery(id+"F0.wireOp",EDGE,"E24.filletArc");Q0=makeQuery(id+"F2.boolean.opBoolean","SPLIT",FACE,{"disambiguationData":[TD([makeQuery(id+"F1.opExtrude","SWEPT_FACE",FACE,{"disambiguationData":[OSD([subQ0])]})])],"derivedFrom":makeQuery(id+"F1.opExtrude","CAP_FACE",FACE,{"disambiguationData":[OSD([subQ0,subQ1,subQ2,subQ3,subQ4,subQ5,subQ6,subQ7,subQ8,subQ9,subQ10,subQ11])],"isStart":true})});}
            var sketch = newSketch(context, id + "F16", { "sketchPlane" : qUnion([Q0])});
            skCircle(sketch, "E79.0", {"center": v(34.05, 185.88) * mm, "radius": 4 * mm});
            skCircle(sketch, "E79.1", {"center": v(154.05, 50.88) * mm, "radius": 4 * mm});
            skCircle(sketch, "E79.2", {"center": v(34.05, 50.88) * mm, "radius": 4 * mm});
            skCircle(sketch, "E79.3", {"center": v(154.05, 185.88) * mm, "radius": 4 * mm});
            skArc(sketch, "E79.4", {"start": v(150.2, 166.56) * mm, "mid": v(94.05, 185.88) * mm, "end": v(37.9, 166.56) * mm});
            skLineSegment(sketch, "E79.5", {"start": v(34.05, 158.68) * mm, "end": v(34.05, 78.09) * mm});
            skArc(sketch, "E79.6", {"start": v(37.9, 166.56) * mm, "mid": v(35.06, 163.06) * mm, "end": v(34.05, 158.68) * mm});
            skArc(sketch, "E79.7", {"start": v(154.05, 158.68) * mm, "mid": v(153.04, 163.06) * mm, "end": v(150.2, 166.56) * mm});
            skLineSegment(sketch, "E79.8", {"start": v(154.05, 158.68) * mm, "end": v(154.05, 78.09) * mm});
            skArc(sketch, "E79.9", {"start": v(150.2, 70.2) * mm, "mid": v(153.04, 73.7) * mm, "end": v(154.05, 78.09) * mm});
            skArc(sketch, "E79.10", {"start": v(37.9, 70.2) * mm, "mid": v(94.05, 50.88) * mm, "end": v(150.2, 70.2) * mm});
            skArc(sketch, "E79.11", {"start": v(34.05, 78.09) * mm, "mid": v(35.06, 73.7) * mm, "end": v(37.9, 70.2) * mm});
            skLineSegment(sketch, "E79.12", {"start": v(14.05, 38.38) * mm, "end": v(14.05, 198.38) * mm});
            skArc(sketch, "E79.13", {"start": v(24.05, 208.38) * mm, "mid": v(16.98, 205.45) * mm, "end": v(14.05, 198.38) * mm});
            skLineSegment(sketch, "E79.14", {"start": v(24.05, 208.38) * mm, "end": v(164.05, 208.38) * mm});
            skArc(sketch, "E79.15", {"start": v(174.05, 198.38) * mm, "mid": v(171.12, 205.45) * mm, "end": v(164.05, 208.38) * mm});
            skLineSegment(sketch, "E79.16", {"start": v(174.05, 38.38) * mm, "end": v(174.05, 198.38) * mm});
            skArc(sketch, "E79.17", {"start": v(164.05, 28.38) * mm, "mid": v(171.12, 31.31) * mm, "end": v(174.05, 38.38) * mm});
            skLineSegment(sketch, "E79.18", {"start": v(24.05, 28.38) * mm, "end": v(164.05, 28.38) * mm});
            skArc(sketch, "E79.19", {"start": v(14.05, 38.38) * mm, "mid": v(16.98, 31.31) * mm, "end": v(24.05, 28.38) * mm});
            skLineSegment(sketch, "E80", {"start": v(94.05, 208.38) * mm, "end": v(94.05, 238.38) * mm, "construction": true});
            skCircle(sketch, "E81", {"center": v(94.05, 238.38) * mm, "radius": 6 * mm});
            skArc(sketch, "E82", {"start": v(109.05, 238.38) * mm, "mid": v(94.05, 253.38) * mm, "end": v(79.05, 238.38) * mm});
            skLineSegment(sketch, "E83", {"start": v(79.05, 238.38) * mm, "end": v(79.05, 226.38) * mm});
            skLineSegment(sketch, "E84", {"start": v(79.05, 226.38) * mm, "end": v(61.05, 208.38) * mm});
            skLineSegment(sketch, "E85", {"start": v(109.05, 238.38) * mm, "end": v(109.05, 226.38) * mm});
            skLineSegment(sketch, "E86", {"start": v(109.05, 226.38) * mm, "end": v(127.05, 208.38) * mm});
            skLineSegment(sketch, "E87", {"start": v(14.05, 118.38) * mm, "end": v(174.05, 118.38) * mm, "construction": true});
            skArc(sketch, "E88.MirrorCS", {"start": v(79.05, 238.38) * mm, "mid": v(94.05, 253.38) * mm, "end": v(109.05, 238.38) * mm});
            skLineSegment(sketch, "E89", {"start": v(61.05, 208.38) * mm, "end": v(127.05, 208.38) * mm});
            skLineSegment(sketch, "E90.MirrorCS", {"start": v(79.05, 10.38) * mm, "end": v(61.05, 28.38) * mm});
            skLineSegment(sketch, "E91.MirrorCS", {"start": v(79.05, -1.62) * mm, "end": v(79.05, 10.38) * mm});
            skCircle(sketch, "E92.MirrorC", {"center": v(94.05, -1.62) * mm, "radius": 6 * mm});
            skArc(sketch, "E93.MirrorCS", {"start": v(79.05, -1.62) * mm, "mid": v(94.05, -16.62) * mm, "end": v(109.05, -1.62) * mm});
            skLineSegment(sketch, "E94.MirrorCS", {"start": v(109.05, -1.62) * mm, "end": v(109.05, 10.38) * mm});
            skLineSegment(sketch, "E95.MirrorCS", {"start": v(109.05, 10.38) * mm, "end": v(127.05, 28.38) * mm});
            skLineSegment(sketch, "E96.MirrorCS", {"start": v(94.05, 28.38) * mm, "end": v(94.05, -1.62) * mm});
            skArc(sketch, "E97.MirrorCS", {"start": v(109.05, -1.62) * mm, "mid": v(94.05, -16.62) * mm, "end": v(79.05, -1.62) * mm});
            skLineSegment(sketch, "E98.MirrorCS", {"start": v(61.05, 28.38) * mm, "end": v(127.05, 28.38) * mm});
            skSolve(sketch);
        }
        {
            var Q0;
            Q0 = qSketchRegion(id + "F16", true);
            var Q1;
            Q1=makeQuery(id+"F2.opExtrude","CAP_FACE",FACE,{"disambiguationData":[OSD([sQuery(id+"F0.wireOp",EDGE,"E12"),sQuery(id+"F0.wireOp",EDGE,"E13"),sQuery(id+"F0.wireOp",EDGE,"E14"),sQuery(id+"F0.wireOp",EDGE,"E15"),sQuery(id+"F0.wireOp",EDGE,"E17.filletArc"),sQuery(id+"F0.wireOp",EDGE,"E18.filletArc"),sQuery(id+"F0.wireOp",EDGE,"E19.filletArc"),sQuery(id+"F0.wireOp",EDGE,"E20.filletArc"),sQuery(id+"F0.wireOp",EDGE,"E25.0"),sQuery(id+"F0.wireOp",EDGE,"E25.1"),sQuery(id+"F0.wireOp",EDGE,"E25.2"),sQuery(id+"F0.wireOp",EDGE,"E25.3"),sQuery(id+"F0.wireOp",EDGE,"E25.4"),sQuery(id+"F0.wireOp",EDGE,"E25.5"),sQuery(id+"F0.wireOp",EDGE,"E25.6"),sQuery(id+"F0.wireOp",EDGE,"E25.7")])],"isStart":false});
            extrude(context, id + "F17", {"entities" : qUnion([Q0]), "endBound" : BoundingType.UP_TO_SURFACE, "endBoundEntityFace" : qUnion([Q1]), "depth" : 25 * mm});
        }
    });
